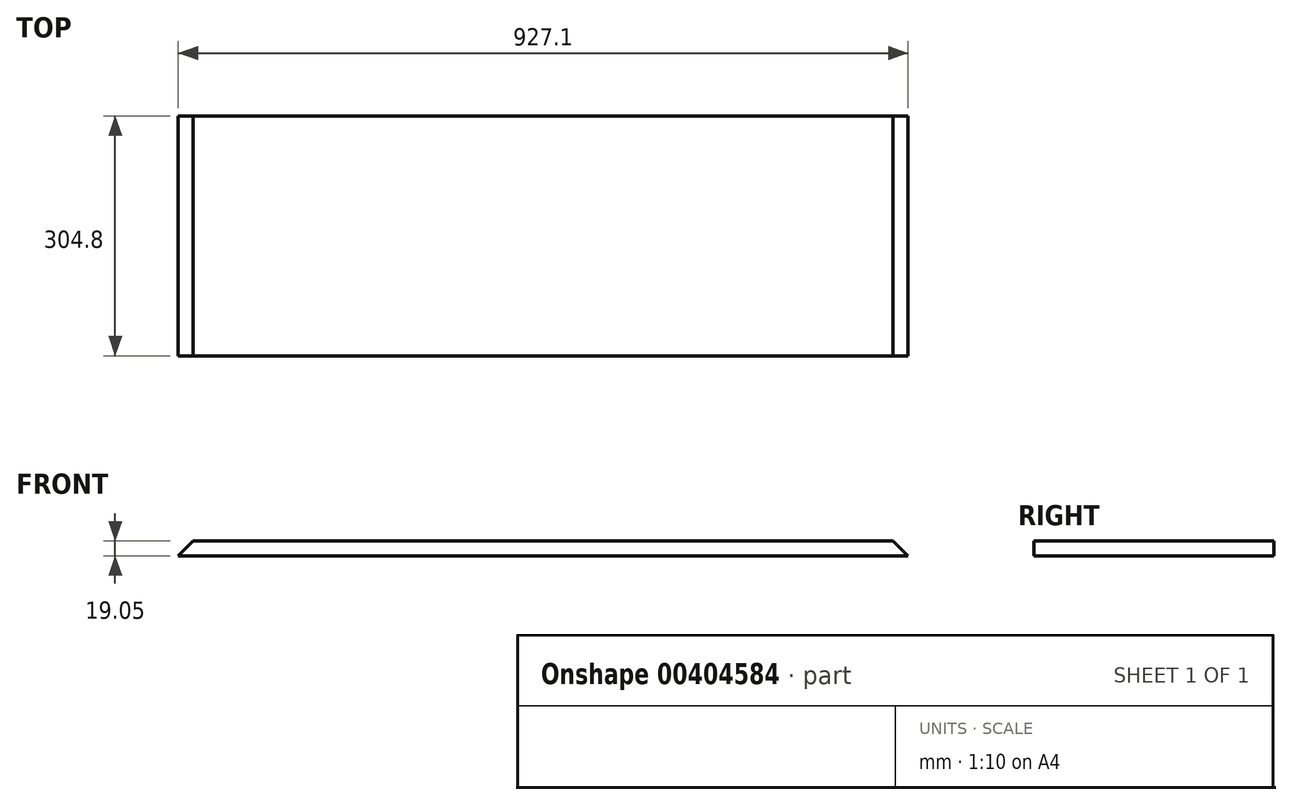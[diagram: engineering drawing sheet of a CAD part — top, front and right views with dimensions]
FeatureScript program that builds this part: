
annotation { "Feature Type Name" : "Feature", "Feature Type Description" : "" }
export const myFeature = defineFeature(function(context is Context, id is Id, definition is map)
    precondition{}
    {
        {
            var Q0;
            Q0=qCreatedBy(makeId("Front.planeOp"),FACE);
            var sketch = newSketch(context, id + "F0", { "sketchPlane" : qUnion([Q0])});
            skLineSegment(sketch, "E0.bottom", {"start": v(-463.55, 0) * mm, "end": v(463.55, 0) * mm});
            skLineSegment(sketch, "E0.top", {"start": v(-444.5, 19.05) * mm, "end": v(444.5, 19.05) * mm});
            skPoint(sketch, "E0.middle", {"position": v(0, 9.53) * mm});
            skLineSegment(sketch, "E1", {"start": v(-463.55, 0) * mm, "end": v(-444.5, 19.05) * mm});
            skLineSegment(sketch, "E2", {"start": v(463.55, 0) * mm, "end": v(444.5, 19.05) * mm});
            skPoint(sketch, "E0.right.end.orphan", {"position": v(463.55, 19.05) * mm});
            skSolve(sketch);
        }
        {
            var Q0;
            Q0=qSketchRegion(id+"F0",true);
            extrude(context, id + "F1", {"entities" : qUnion([Q0]), "endBound" : BoundingType.SYMMETRIC, "depth" : 304.8 * mm});
        }
    });
